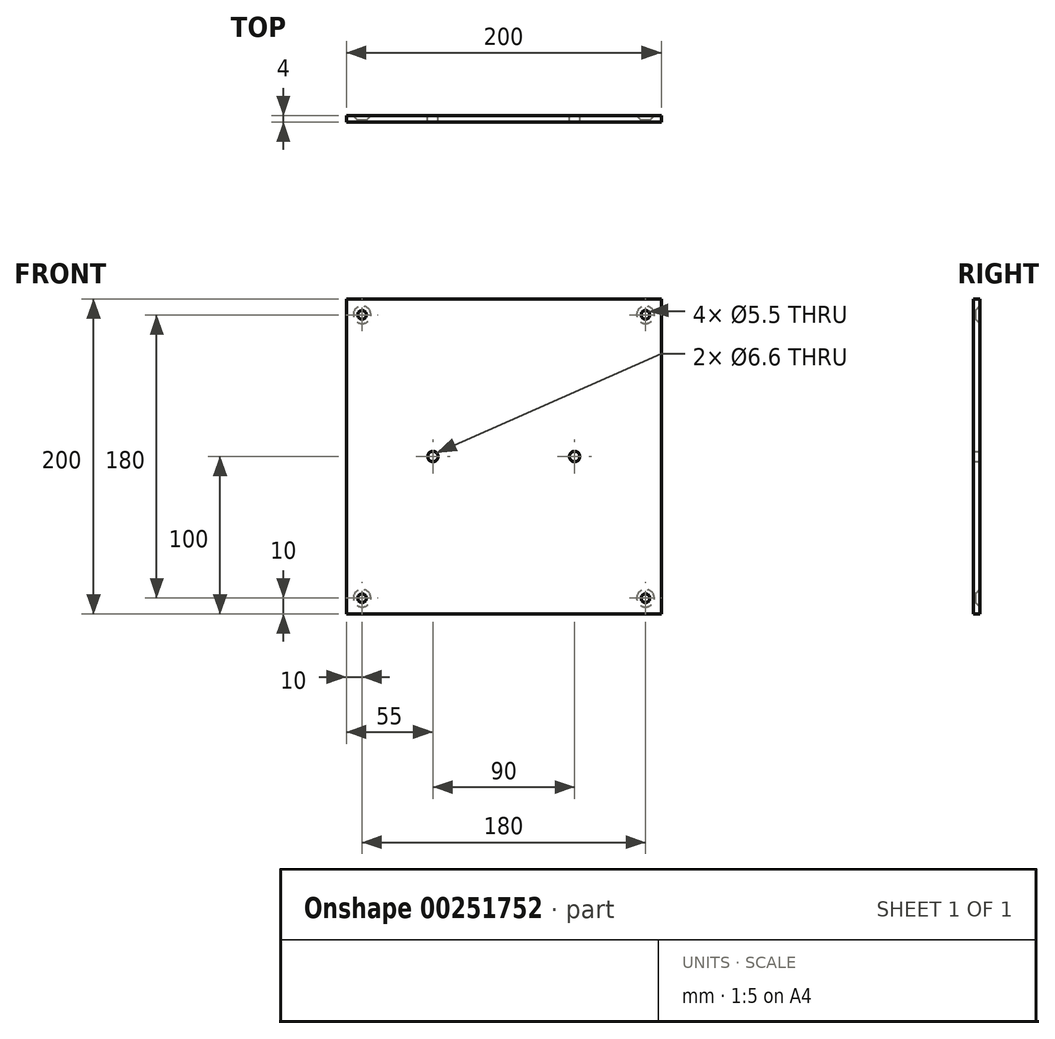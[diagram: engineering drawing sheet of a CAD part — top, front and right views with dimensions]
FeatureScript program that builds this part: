
annotation { "Feature Type Name" : "Feature", "Feature Type Description" : "" }
export const myFeature = defineFeature(function(context is Context, id is Id, definition is map)
    precondition{}
    {
        {
            var Q0;
            Q0=qCreatedBy(makeId("Front.planeOp"),FACE);
            var sketch = newSketch(context, id + "F0", { "sketchPlane" : qUnion([Q0])});
            skLineSegment(sketch, "E0.bottom", {"start": v(100, -100) * mm, "end": v(-100, -100) * mm});
            skLineSegment(sketch, "E0.top", {"start": v(100, 100) * mm, "end": v(-100, 100) * mm});
            skLineSegment(sketch, "E0.left", {"start": v(100, -100) * mm, "end": v(100, 100) * mm});
            skLineSegment(sketch, "E0.right", {"start": v(-100, -100) * mm, "end": v(-100, 100) * mm});
            skPoint(sketch, "E0.middle", {"position": v(0, 0) * mm});
            skPoint(sketch, "E1", {"position": v(-90, 90) * mm});
            skPoint(sketch, "E2", {"position": v(90, 90) * mm});
            skPoint(sketch, "E3", {"position": v(-90, -90) * mm});
            skPoint(sketch, "E4", {"position": v(90, -90) * mm});
            skPoint(sketch, "E5", {"position": v(45, 0) * mm});
            skPoint(sketch, "E6", {"position": v(-45, 0) * mm});
            skSolve(sketch);
        }
        {
            var Q0;
            Q0 = qSketchRegion(id + "F0", true);
            extrude(context, id + "F1", {"entities" : qUnion([Q0]), "depth" : 4 * mm});
        }
        {
            var Q0;
            Q0=sQuery(id+"F0.wireOp",VERTEX,"E6");
            var Q1;
            Q1=sQuery(id+"F0.wireOp",VERTEX,"E5");
            var Q2;
            Q2=makeQuery(id+"F1.opExtrude","SWEPT_BODY",BODY,{"disambiguationData":[OSD([sQuery(id+"F0.wireOp",EDGE,"E0.bottom"),sQuery(id+"F0.wireOp",EDGE,"E0.top"),sQuery(id+"F0.wireOp",EDGE,"E0.left"),sQuery(id+"F0.wireOp",EDGE,"E0.right")])]});
            hole(context, id + "F2", {"style" : HoleStyle.SIMPLE, "endStyle" : HoleEndStyle.THROUGH, "oppositeDirection" : true, "standardTappedOrClearance" : lookupTablePath({ "standard" : "ISO", "fit" : "Normal", "size" : "M6", "type" : "Clearance" }), "standardBlindInLast" : lookupTablePath({ "fit" : "Standard", "standard" : "ISO", "size" : "M6", "type" : "Clearance" }), "holeDiameter" : 6.6 * mm, "isTappedThrough" : true, "tappedDepth" : 12 * mm, "tapClearance" : 3, "locations" : qUnion([Q0, Q1]), "scope" : qUnion([Q2])});
        }
        {
            var Q0;
            Q0=sQuery(id+"F0.wireOp",VERTEX,"E1");
            var Q1;
            Q1=sQuery(id+"F0.wireOp",VERTEX,"E2");
            var Q2;
            Q2=sQuery(id+"F0.wireOp",VERTEX,"E3");
            var Q3;
            Q3=sQuery(id+"F0.wireOp",VERTEX,"E4");
            var Q4;
            Q4=makeQuery(id+"F1.opExtrude","SWEPT_BODY",BODY,{"disambiguationData":[OSD([sQuery(id+"F0.wireOp",EDGE,"E0.bottom"),sQuery(id+"F0.wireOp",EDGE,"E0.top"),sQuery(id+"F0.wireOp",EDGE,"E0.left"),sQuery(id+"F0.wireOp",EDGE,"E0.right")])]});
            hole(context, id + "F3", {"style" : HoleStyle.C_SINK, "endStyle" : HoleEndStyle.THROUGH, "oppositeDirection" : true, "standardTappedOrClearance" : lookupTablePath({ "standard" : "ISO", "fit" : "Normal", "size" : "M5", "type" : "Clearance" }), "standardBlindInLast" : lookupTablePath({ "fit" : "Standard", "standard" : "ISO", "size" : "M5", "type" : "Clearance" }), "holeDiameter" : 5.5 * mm, "cSinkDiameter" : 11.2 * mm, "cSinkAngle" : 90 * degree, "isTappedThrough" : true, "tappedDepth" : 12 * mm, "tapClearance" : 3, "locations" : qUnion([Q0, Q1, Q2, Q3]), "scope" : qUnion([Q4])});
        }
    });
